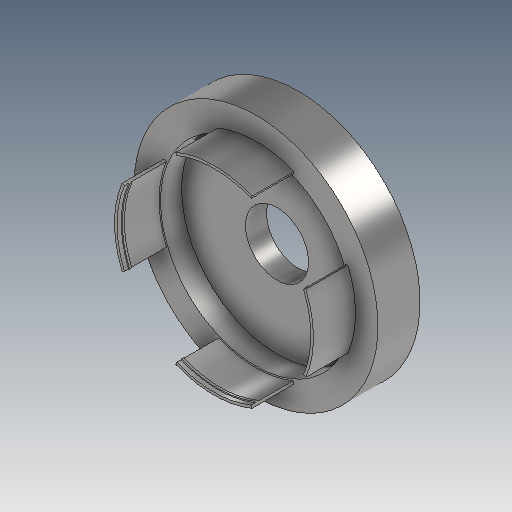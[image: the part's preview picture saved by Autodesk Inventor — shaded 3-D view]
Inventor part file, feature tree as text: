
AUTODESK INVENTOR PART (.ipt)
format: ipt  version: 2020.3 (Build 243373010, 373A)  size: 249,856 bytes
history: native  units: mm
features: sketch x6, extrude x5, plane x1, pattern_circular x1, hole x1
ambient origin geometry x8: Origin, YZ Plane, XZ Plane, XY Plane, X Axis, Y Axis, Z Axis, Center Point
bodies: Solid1 (feature_tree)
feature tree (14):
  extrude  "Extrusion1"  Depth=45.4mm
  extrude  "Extrusion2"  Depth=15.0mm
  extrude  "Extrusion3"  Depth=5.0mm
  plane  "Work Plane2"
  extrude  "Extrusion4"  TaperAngle=45.0deg  [1 undecoded]
  pattern_circular  "Circular Pattern1"  Count=4 Angle=360.0deg
  extrude  "Extrusion5"  Depth=10.0mm
  hole  "Hole1"  [1 undecoded]
  sketch  "Sketch1"  dims[d0=48.0mm d1=45.4mm]
  sketch  "Sketch2"  dims[d2=5.0mm d3=0.0mm d4=15.0mm]
  sketch  "Sketch3"  dims[d5=5.0mm d6=0.0mm d7=0.35mm]
  sketch  "Sketch6"  dims[d8=0.35mm d9=45.0deg d10=22.5deg d11=40.0mm d13=360.0deg]
  sketch  "Sketch7"  dims[d15=10.0mm d16=0.0mm d19=0.25mm]
  sketch  "Sketch8"  dims[d20=-1.25mm d21=0.5mm d22=0.0mm d23=40.0mm d24=360.0deg d26=58.0mm d27=10.0mm d28=0.0mm d29=2.459mm d30=6.0mm d31=6.0mm d32=2.0mm d33=90.0deg d34=8.8mm d35=0.0mm]
note: 2 required parameter values undecoded (feature->parameter linkage not recoverable at this tier; creation-order binding heuristic only, values carry confidence <= 0.55)
